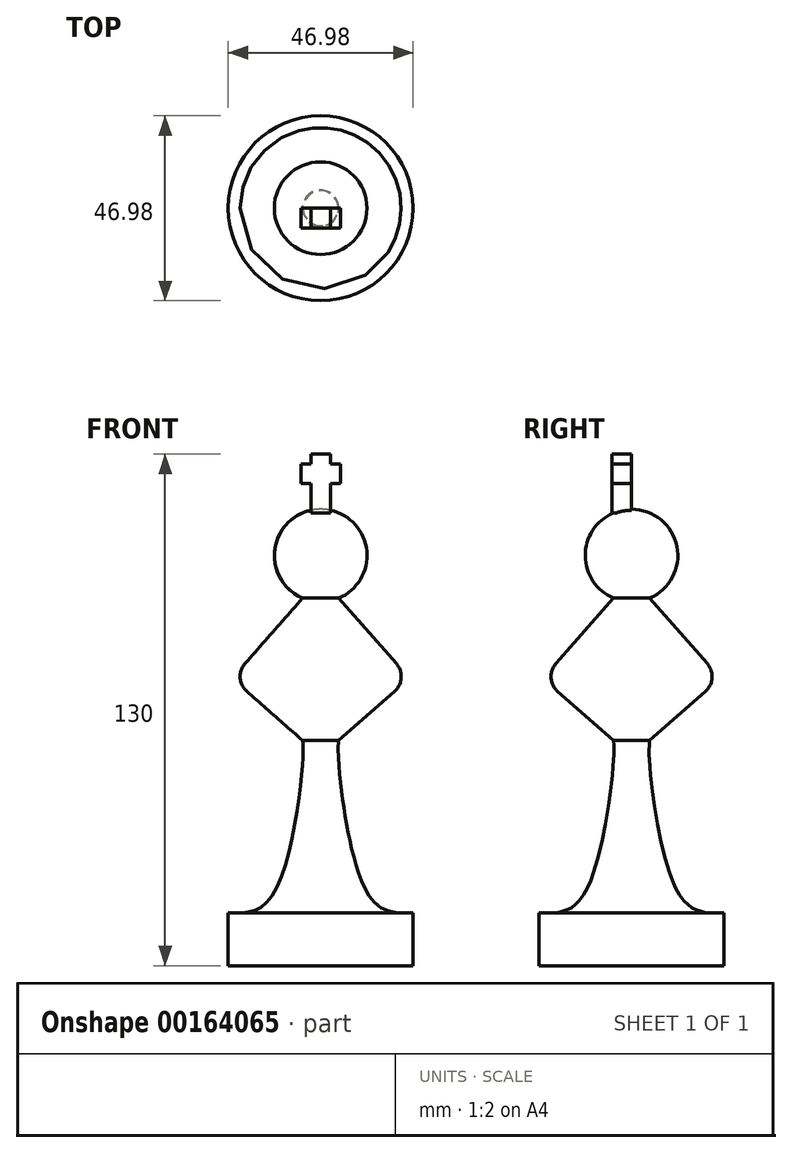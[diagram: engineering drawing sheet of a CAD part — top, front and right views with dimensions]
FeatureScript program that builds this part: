
annotation { "Feature Type Name" : "Feature", "Feature Type Description" : "" }
export const myFeature = defineFeature(function(context is Context, id is Id, definition is map)
    precondition{}
    {
        {
            var Q0;
            Q0=qCreatedBy(makeId("Front.planeOp"),FACE);
            var sketch = newSketch(context, id + "F0", { "sketchPlane" : qUnion([Q0])});
            skLineSegment(sketch, "E0.bottom", {"start": v(-2.5, 130) * mm, "end": v(2.5, 130) * mm});
            skLineSegment(sketch, "E0.top", {"start": v(-2.5, 115) * mm, "end": v(2.5, 115) * mm});
            skLineSegment(sketch, "E0.left", {"start": v(-2.5, 130) * mm, "end": v(-2.5, 115) * mm});
            skLineSegment(sketch, "E0.right", {"start": v(2.5, 130) * mm, "end": v(2.5, 115) * mm});
            skSolve(sketch);
        }
        {
            var Q0;
            Q0 = qSketchRegion(id + "F0", true);
            extrude(context, id + "F1", {"entities" : qUnion([Q0]), "depth" : 5 * mm});
        }
        {
            var Q0;
            Q0=qCreatedBy(makeId("Front.planeOp"),FACE);
            var sketch = newSketch(context, id + "F2", { "sketchPlane" : qUnion([Q0])});
            skLineSegment(sketch, "E1.bottom", {"start": v(-5, 127.5) * mm, "end": v(5, 127.5) * mm});
            skLineSegment(sketch, "E1.top", {"start": v(-5, 122.5) * mm, "end": v(5, 122.5) * mm});
            skLineSegment(sketch, "E1.left", {"start": v(-5, 127.5) * mm, "end": v(-5, 122.5) * mm});
            skLineSegment(sketch, "E1.right", {"start": v(5, 127.5) * mm, "end": v(5, 122.5) * mm});
            skSolve(sketch);
        }
        {
            var Q0;
            Q0 = qSketchRegion(id + "F2", true);
            extrude(context, id + "F3", {"entities" : qUnion([Q0]), "operationType" : NewBodyOperationType.ADD, "depth" : 5 * mm});
        }
        {
            var Q0;
            Q0=qCreatedBy(makeId("Front.planeOp"),FACE);
            var sketch = newSketch(context, id + "F4", { "sketchPlane" : qUnion([Q0])});
            skArc(sketch, "E2", {"start": v(0, 116) * mm, "mid": v(-11.53, 106.57) * mm, "end": v(-4.58, 93.4) * mm});
            skLineSegment(sketch, "E3", {"start": v(-4.58, 93.4) * mm, "end": v(-22.52, 73.03) * mm});
            skLineSegment(sketch, "E4", {"start": v(-22.52, 73.03) * mm, "end": v(-4.58, 57.22) * mm});
            skFitSpline(sketch, "E5", {"points": [v(-4.58, 57.22) * mm, v(-4.58, 51.8) * mm, v(-12.87, 17.04) * mm, v(-23.49, 13.5) * mm], "startDerivative": vector(1.5, -17.88) * mm, "endDerivative": vector(-40.02, 1.88) * mm});
            skLineSegment(sketch, "E6", {"start": v(-23.49, 13.5) * mm, "end": v(-23.49, 0) * mm});
            skLineSegment(sketch, "E7", {"start": v(-23.49, 0) * mm, "end": v(0, 0) * mm});
            skLineSegment(sketch, "E8", {"start": v(0, 0) * mm, "end": v(0, 116) * mm});
            skSolve(sketch);
        }
        {
            var Q0;
            Q0 = qSketchRegion(id + "F4", true);
            var Q1;
            Q1=sQuery(id+"F4.wireOp",EDGE,"E8");
            revolve(context, id + "F5", {"operationType" : NewBodyOperationType.ADD, "entities" : qUnion([Q0]), "axis" : qUnion([Q1]), "revolveType" : RevolveType.FULL});
        }
        {
            var Q0;
            Q0=makeQuery(id+"F5.opRevolve","SWEPT_EDGE",EDGE,{"disambiguationData":[OSD([sQuery(id+"F4.wireOp",EDGE,"E3"),sQuery(id+"F4.wireOp",EDGE,"E4")])]});
            fillet(context, id + "F6", {"entities" : qUnion([Q0]), "radius" : 5 * mm, "tangentPropagation" : true, "allowEdgeOverflow" : false});
        }
    });
